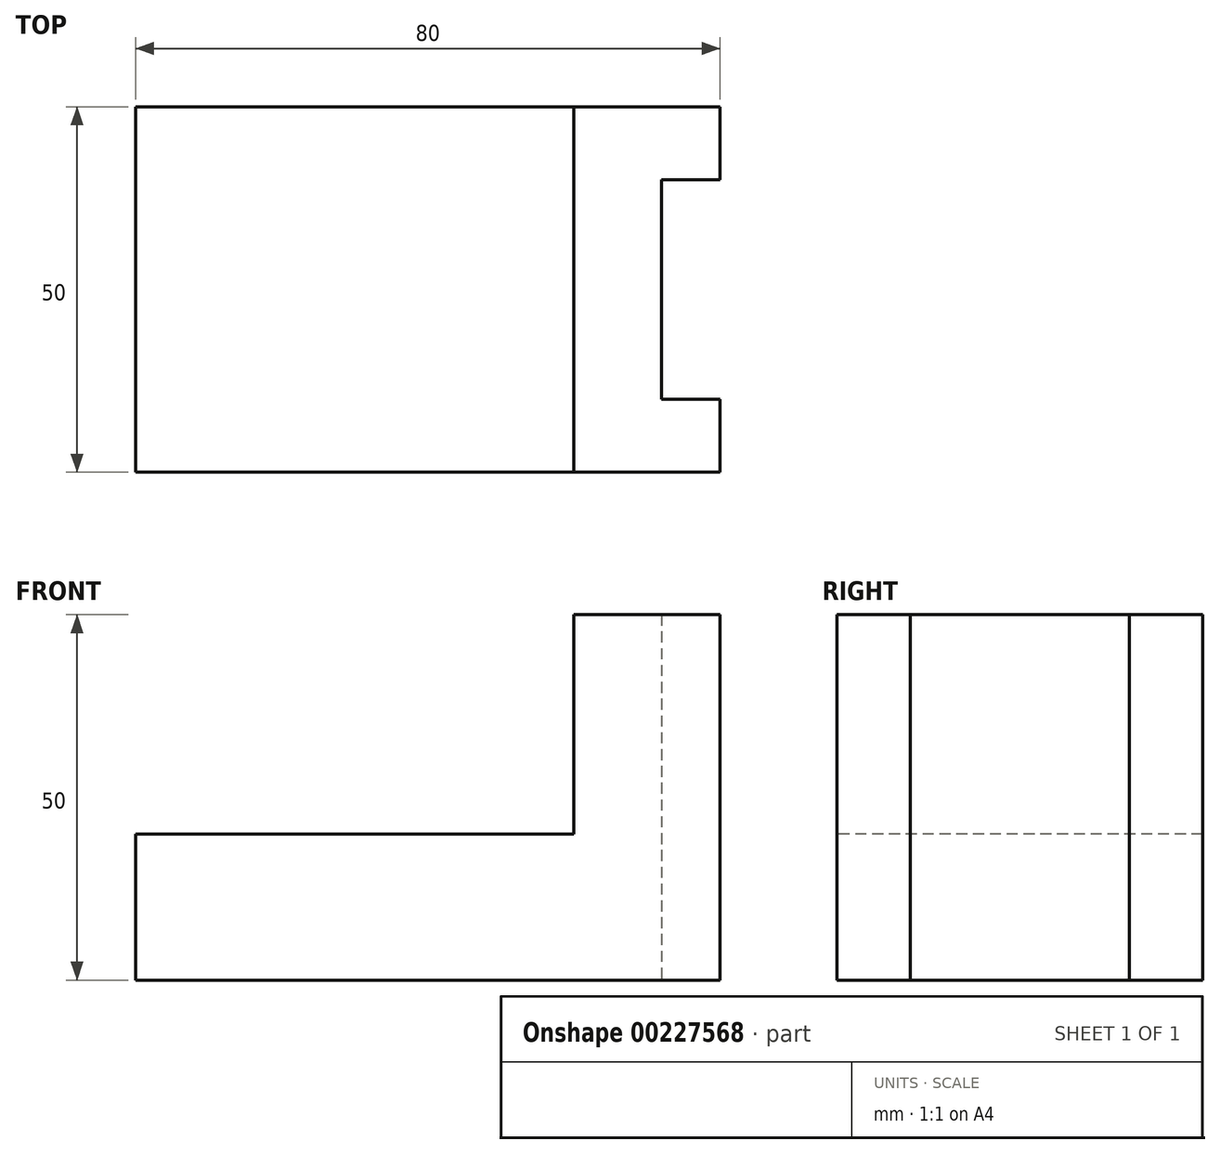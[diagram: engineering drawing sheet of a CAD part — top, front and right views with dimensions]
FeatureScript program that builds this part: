
annotation { "Feature Type Name" : "Feature", "Feature Type Description" : "" }
export const myFeature = defineFeature(function(context is Context, id is Id, definition is map)
    precondition{}
    {
        {
            var Q0;
            Q0=qCreatedBy(makeId("Top.planeOp"),FACE);
            var sketch = newSketch(context, id + "F0", { "sketchPlane" : qUnion([Q0])});
            skLineSegment(sketch, "E0.bottom", {"start": v(-33.55, 25.48) * mm, "end": v(26.45, 25.48) * mm});
            skLineSegment(sketch, "E0.top", {"start": v(-33.55, -24.52) * mm, "end": v(26.45, -24.52) * mm});
            skLineSegment(sketch, "E0.left", {"start": v(-33.55, 25.48) * mm, "end": v(-33.55, -24.52) * mm});
            skLineSegment(sketch, "E0.right", {"start": v(26.45, 25.48) * mm, "end": v(26.45, -24.52) * mm});
            skLineSegment(sketch, "E1.left", {"start": v(26.45, 25.48) * mm, "end": v(26.45, 25.48) * mm});
            skLineSegment(sketch, "E2.bottom", {"start": v(26.45, 25.48) * mm, "end": v(46.45, 25.48) * mm});
            skLineSegment(sketch, "E2.top", {"start": v(26.45, -24.52) * mm, "end": v(46.45, -24.52) * mm});
            skLineSegment(sketch, "E2.right", {"start": v(46.45, 25.48) * mm, "end": v(46.45, 15.48) * mm});
            skLineSegment(sketch, "E3.bottom", {"start": v(46.45, -14.52) * mm, "end": v(38.45, -14.52) * mm});
            skLineSegment(sketch, "E3.top", {"start": v(46.45, 15.48) * mm, "end": v(38.45, 15.48) * mm});
            skLineSegment(sketch, "E3.right", {"start": v(38.45, -14.52) * mm, "end": v(38.45, 15.48) * mm});
            skLineSegment(sketch, "E4.trimOffspring", {"start": v(46.45, -14.52) * mm, "end": v(46.45, -24.52) * mm});
            skSolve(sketch);
        }
        {
            var Q0;
            Q0=makeQuery(id+"F0.imprint","IMPRINT",FACE,{"disambiguationData":[TD([[makeQuery(id+"F0.imprint","IMPRINT",EDGE,{"derivedFrom":sQuery(id+"F0.wireOp",EDGE,"E0.bottom")}),-1.0]])]});
            extrude(context, id + "F1", {"entities" : qUnion([Q0]), "depth" : 20 * mm});
        }
        {
            var Q0;
            Q0=makeQuery(id+"F0.imprint","IMPRINT",FACE,{"disambiguationData":[TD([[makeQuery(id+"F0.imprint","IMPRINT",EDGE,{"derivedFrom":sQuery(id+"F0.wireOp",EDGE,"E2.bottom")}),-1.0]])]});
            extrude(context, id + "F2", {"entities" : qUnion([Q0]), "operationType" : NewBodyOperationType.ADD, "depth" : 50 * mm});
        }
    });
